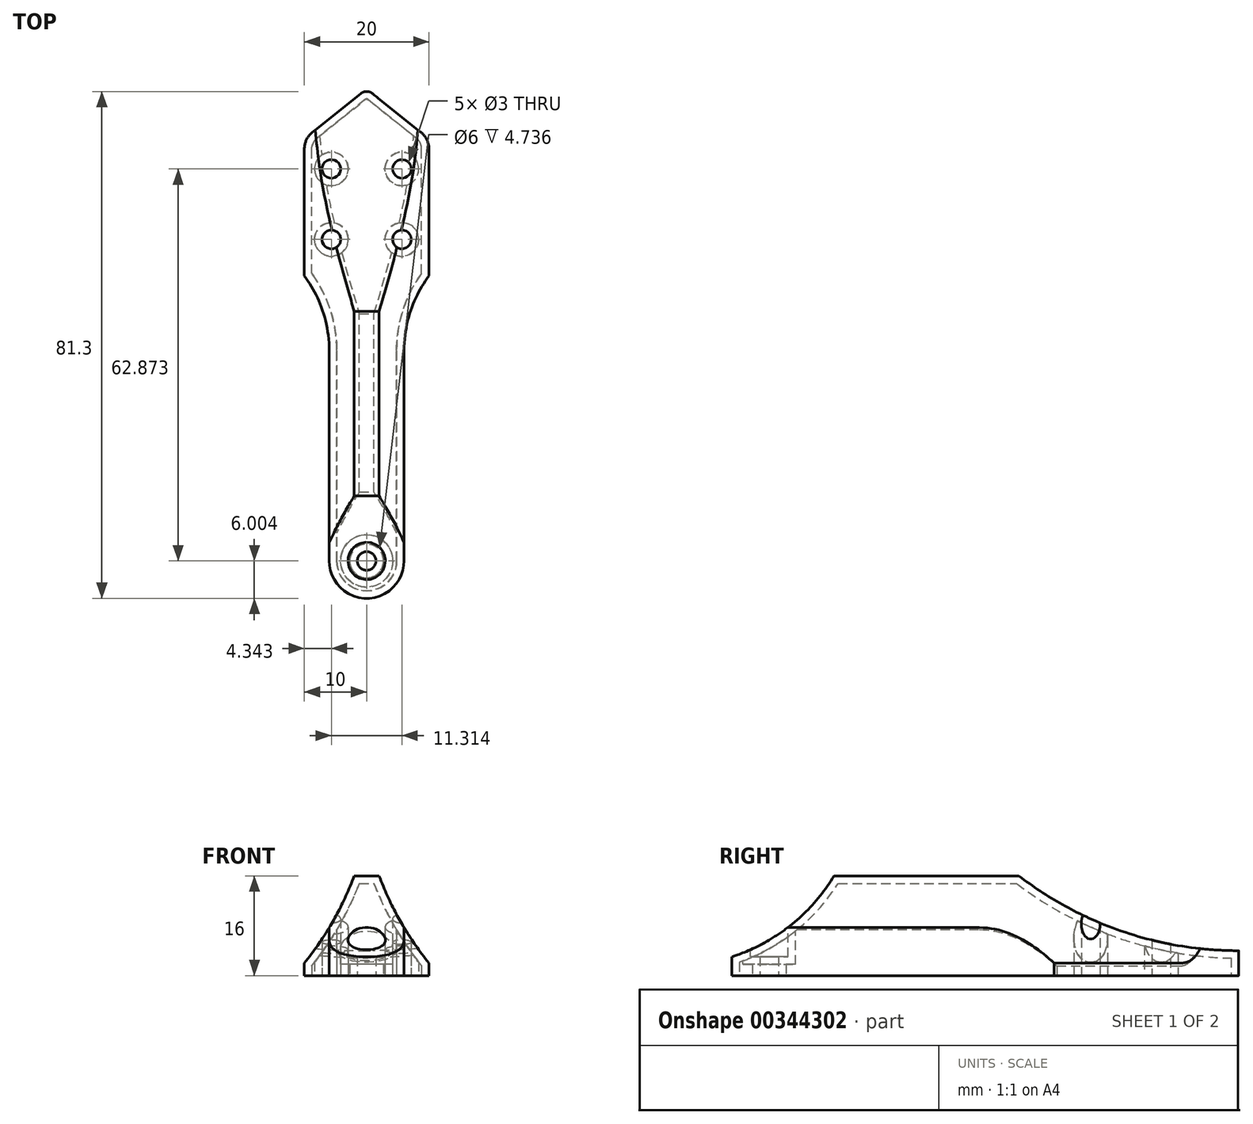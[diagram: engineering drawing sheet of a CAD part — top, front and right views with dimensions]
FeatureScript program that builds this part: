
annotation { "Feature Type Name" : "Feature", "Feature Type Description" : "" }
export const myFeature = defineFeature(function(context is Context, id is Id, definition is map)
    precondition{}
    {
        {
            var Q0;
            Q0=qCreatedBy(makeId("Top.planeOp"),FACE);
            var sketch = newSketch(context, id + "F0", { "sketchPlane" : qUnion([Q0])});
            skLineSegment(sketch, "E0", {"start": v(0, 72.7) * mm, "end": v(0, -98.78) * mm, "construction": true});
            skLineSegment(sketch, "E1.0", {"start": v(6, -23.5) * mm, "end": v(6, -57.22) * mm});
            skCircle(sketch, "E2", {"center": v(0, 0) * mm, "radius": 4 * mm});
            skLineSegment(sketch, "E3.0", {"start": v(10, 8.82) * mm, "end": v(10, -11.5) * mm});
            skCircle(sketch, "E4", {"center": v(0, 0) * mm, "radius": 8 * mm, "construction": true});
            skLineSegment(sketch, "E5", {"start": v(0, 0) * mm, "end": v(-5.66, 5.66) * mm, "construction": true});
            skCircle(sketch, "E6", {"center": v(-5.66, 5.66) * mm, "radius": 1.5 * mm});
            skLineSegment(sketch, "E7", {"start": v(0.94, 17.75) * mm, "end": v(8.69, 11.55) * mm});
            skArc(sketch, "E8", {"start": v(10, -11.5) * mm, "mid": v(7.03, -17.18) * mm, "end": v(6, -23.5) * mm});
            skCircle(sketch, "E9.1.0", {"center": v(-5.66, -5.66) * mm, "radius": 1.5 * mm});
            skCircle(sketch, "E9.2.0", {"center": v(5.66, -5.66) * mm, "radius": 1.5 * mm});
            skCircle(sketch, "E10.1.3.0", {"center": v(5.66, 5.66) * mm, "radius": 1.5 * mm});
            skLineSegment(sketch, "E11", {"start": v(0, 10.5) * mm, "end": v(3.06, 10.5) * mm});
            skLineSegment(sketch, "E12", {"start": v(3.53, 11.84) * mm, "end": v(0.62, 14.16) * mm});
            skCircle(sketch, "E13", {"center": v(0, -57.22) * mm, "radius": 1.5 * mm});
            skLineSegment(sketch, "E14", {"start": v(0, 0) * mm, "end": v(49.4, -49.4) * mm, "construction": true});
            skLineSegment(sketch, "E15", {"start": v(49.4, -49.4) * mm, "end": v(0, -98.78) * mm, "construction": true});
            skLineSegment(sketch, "E16", {"start": v(0, -77.22) * mm, "end": v(10.78, -88) * mm, "construction": true});
            skLineSegment(sketch, "E17.MirrorCS", {"start": v(-6, -23.5) * mm, "end": v(-6, -57.22) * mm});
            skArc(sketch, "E18.MirrorCS", {"start": v(-10, -11.5) * mm, "mid": v(-7.03, -17.18) * mm, "end": v(-6, -23.5) * mm});
            skLineSegment(sketch, "E19.MirrorCS", {"start": v(-10, 8.82) * mm, "end": v(-10, -11.5) * mm});
            skLineSegment(sketch, "E20.MirrorCS", {"start": v(-0.94, 17.75) * mm, "end": v(-8.69, 11.55) * mm});
            skLineSegment(sketch, "E21.MirrorCS", {"start": v(-3.53, 11.84) * mm, "end": v(-0.62, 14.16) * mm});
            skLineSegment(sketch, "E22.MirrorCS", {"start": v(0, 10.5) * mm, "end": v(-3.06, 10.5) * mm});
            skPoint(sketch, "E23.visualSharp", {"position": v(-5.2, 10.5) * mm});
            skArc(sketch, "E23.filletArc", {"start": v(-3.53, 11.84) * mm, "mid": v(-3.77, 11) * mm, "end": v(-3.06, 10.5) * mm});
            skPoint(sketch, "E24.visualSharp", {"position": v(5.2, 10.5) * mm});
            skArc(sketch, "E24.filletArc", {"start": v(3.06, 10.5) * mm, "mid": v(3.77, 11) * mm, "end": v(3.53, 11.84) * mm});
            skPoint(sketch, "E25.visualSharp", {"position": v(0, 14.66) * mm});
            skArc(sketch, "E25.filletArc", {"start": v(0.62, 14.16) * mm, "mid": v(0, 14.38) * mm, "end": v(-0.62, 14.16) * mm});
            skPoint(sketch, "E26.visualSharp", {"position": v(0, 18.5) * mm});
            skArc(sketch, "E26.filletArc", {"start": v(0.94, 17.75) * mm, "mid": v(0, 18.08) * mm, "end": v(-0.94, 17.75) * mm});
            skPoint(sketch, "E27.visualSharp", {"position": v(10, 10.5) * mm});
            skArc(sketch, "E27.filletArc", {"start": v(10, 8.82) * mm, "mid": v(9.65, 10.33) * mm, "end": v(8.69, 11.55) * mm});
            skPoint(sketch, "E28.visualSharp", {"position": v(-10, 10.5) * mm});
            skArc(sketch, "E28.filletArc", {"start": v(-8.69, 11.55) * mm, "mid": v(-9.65, 10.33) * mm, "end": v(-10, 8.82) * mm});
            skLineSegment(sketch, "E29.bottom", {"start": v(-68.1, 57.26) * mm, "end": v(73.4, 57.26) * mm});
            skLineSegment(sketch, "E29.top", {"start": v(-68.1, -109.53) * mm, "end": v(73.4, -109.53) * mm});
            skLineSegment(sketch, "E29.left", {"start": v(-68.1, 57.26) * mm, "end": v(-68.1, -109.53) * mm});
            skLineSegment(sketch, "E29.right", {"start": v(73.4, 57.26) * mm, "end": v(73.4, -109.53) * mm});
            skLineSegment(sketch, "E30", {"start": v(0, -50.14) * mm, "end": v(-6, -56.14) * mm});
            skArc(sketch, "E31.trimOffspring", {"start": v(-6, -57.22) * mm, "mid": v(0, -63.22) * mm, "end": v(6, -57.22) * mm});
            skLineSegment(sketch, "E32", {"start": v(-6, -52.6) * mm, "end": v(0, -46.6) * mm});
            skLineSegment(sketch, "E33.MirrorCS", {"start": v(6, -52.6) * mm, "end": v(0, -46.6) * mm});
            skLineSegment(sketch, "E34.MirrorCS", {"start": v(0, -50.14) * mm, "end": v(6, -56.14) * mm});
            skSolve(sketch);
        }
        {
            var Q0;
            Q0=qCreatedBy(makeId("Front.planeOp"),FACE);
            var sketch = newSketch(context, id + "F1", { "sketchPlane" : qUnion([Q0])});
            skLineSegment(sketch, "E35", {"start": v(0, 0) * mm, "end": v(0, 16) * mm, "construction": true});
            skLineSegment(sketch, "E36", {"start": v(-10, 0) * mm, "end": v(-10, 2) * mm});
            skLineSegment(sketch, "E37", {"start": v(-2, 16) * mm, "end": v(0, 16) * mm});
            skLineSegment(sketch, "E38.MirrorCS", {"start": v(10, 0) * mm, "end": v(10, 2) * mm});
            skLineSegment(sketch, "E39.MirrorCS", {"start": v(2, 16) * mm, "end": v(0, 16) * mm});
            skLineSegment(sketch, "E40", {"start": v(10, 0) * mm, "end": v(-10, 0) * mm});
            skArc(sketch, "E41", {"start": v(2, 16) * mm, "mid": v(5.43, 8.68) * mm, "end": v(10, 2) * mm});
            skArc(sketch, "E42.MirrorCS", {"start": v(-2, 16) * mm, "mid": v(-5.43, 8.68) * mm, "end": v(-10, 2) * mm});
            skSolve(sketch);
        }
        {
            var Q0;
            Q0 = qSketchRegion(id + "F1", true);
            extrude(context, id + "F2", {"entities" : qUnion([Q0]), "depth" : 100 * mm, "hasSecondDirection" : true, "secondDirectionOppositeDirection" : true, "secondDirectionDepth" : 25 * mm});
        }
        {
            var Q0;
            Q0=makeQuery(id+"F0.imprint","IMPRINT",FACE,{"disambiguationData":[TD([[makeQuery(id+"F0.imprint","IMPRINT",EDGE,{"derivedFrom":sQuery(id+"F0.wireOp",EDGE,"E1.0")}),1.0]])]});
            var Q1;
            Q1=makeQuery(id+"F0.imprint","IMPRINT",FACE,{"disambiguationData":[TD([[makeQuery(id+"F0.imprint","IMPRINT",EDGE,{"derivedFrom":sQuery(id+"F0.wireOp",EDGE,"E10.1.3.0")}),1.0]])]});
            var Q2;
            Q2=makeQuery(id+"F0.imprint","IMPRINT",FACE,{"disambiguationData":[TD([[makeQuery(id+"F0.imprint","IMPRINT",EDGE,{"derivedFrom":sQuery(id+"F0.wireOp",EDGE,"E6")}),1.0]])]});
            var Q3;
            Q3=makeQuery(id+"F0.imprint","IMPRINT",FACE,{"disambiguationData":[TD([[makeQuery(id+"F0.imprint","IMPRINT",EDGE,{"derivedFrom":sQuery(id+"F0.wireOp",EDGE,"E9.1.0")}),1.0]])]});
            var Q4;
            Q4=makeQuery(id+"F0.imprint","IMPRINT",FACE,{"disambiguationData":[TD([[makeQuery(id+"F0.imprint","IMPRINT",EDGE,{"derivedFrom":sQuery(id+"F0.wireOp",EDGE,"E9.2.0")}),1.0]])]});
            var Q5;
            Q5=makeQuery(id+"F0.imprint","IMPRINT",FACE,{"disambiguationData":[TD([[makeQuery(id+"F0.imprint","IMPRINT",EDGE,{"derivedFrom":sQuery(id+"F0.wireOp",EDGE,"E13")}),1.0]])]});
            extrude(context, id + "F3", {"entities" : qUnion([Q0, Q1, Q2, Q3, Q4, Q5]), "operationType" : NewBodyOperationType.REMOVE, "depth" : 25 * mm});
        }
        {
            var Q0;
            Q0=qCreatedBy(makeId("Right.planeOp"),FACE);
            var sketch = newSketch(context, id + "F4", { "sketchPlane" : qUnion([Q0])});
            skLineSegment(sketch, "E43.0.0", {"start": v(16.9, 16) * mm, "end": v(16.9, 16) * mm});
            skLineSegment(sketch, "E43.0.5", {"start": v(17.75, 16) * mm, "end": v(16.9, 16) * mm});
            skArc(sketch, "E44", {"start": v(18.08, 4) * mm, "mid": v(-0.54, 7.08) * mm, "end": v(-17.18, 16) * mm});
            skLineSegment(sketch, "E45", {"start": v(18.08, 4) * mm, "end": v(18.08, 16) * mm});
            skLineSegment(sketch, "E46", {"start": v(18.08, 16) * mm, "end": v(-17.18, 16) * mm});
            skPoint(sketch, "E47.0", {"position": v(-63.22, 16) * mm});
            skArc(sketch, "E48", {"start": v(-63.22, 3) * mm, "mid": v(-53.84, 8.02) * mm, "end": v(-46.81, 16) * mm});
            skLineSegment(sketch, "E49", {"start": v(-63.22, 16) * mm, "end": v(-63.22, 3) * mm});
            skLineSegment(sketch, "E50", {"start": v(-63.22, 16) * mm, "end": v(-46.81, 16) * mm});
            skLineSegment(sketch, "E51", {"start": v(-63.22, 16) * mm, "end": v(-67.33, 16) * mm});
            skLineSegment(sketch, "E52", {"start": v(-67.33, 16) * mm, "end": v(-67.33, 3) * mm});
            skLineSegment(sketch, "E53", {"start": v(-67.33, 3) * mm, "end": v(-63.22, 3) * mm});
            skSolve(sketch);
        }
        {
            var Q0;
            Q0 = qSketchRegion(id + "F4", true);
            extrude(context, id + "F5", {"entities" : qUnion([Q0]), "operationType" : NewBodyOperationType.REMOVE, "oppositeDirection" : true, "depth" : 25 * mm, "hasSecondDirection" : true, "secondDirectionOppositeDirection" : false, "secondDirectionDepth" : 25 * mm});
        }
        {
            var Q0;
            Q0=makeQuery(id+"F2.opExtrude","SWEPT_FACE",FACE,{"disambiguationData":[OSD([sQuery(id+"F1.wireOp",EDGE,"E37"),sQuery(id+"F1.wireOp",EDGE,"E39.MirrorCS")])]});
            var sketch = newSketch(context, id + "F6", { "sketchPlane" : qUnion([Q0])});
            skCircle(sketch, "E54.0", {"center": v(0, -57.22) * mm, "radius": 1.5 * mm});
            skCircle(sketch, "E55", {"center": v(0, -57.22) * mm, "radius": 3 * mm});
            skSolve(sketch);
        }
        {
            var Q0;
            Q0 = qSketchRegion(id + "F6", true);
            extrude(context, id + "F7", {"entities" : qUnion([Q0]), "operationType" : NewBodyOperationType.REMOVE, "oppositeDirection" : true, "depth" : 13 * mm});
        }
        {
            var Q0;
            Q0=makeQuery(id+"F2.opExtrude","SWEPT_FACE",FACE,{"disambiguationData":[OSD([sQuery(id+"F1.wireOp",EDGE,"E40")])]});
            shell(context, id + "F8", {"entities" : qUnion([Q0]), "thickness" : 1.2 * mm});
        }
    });
